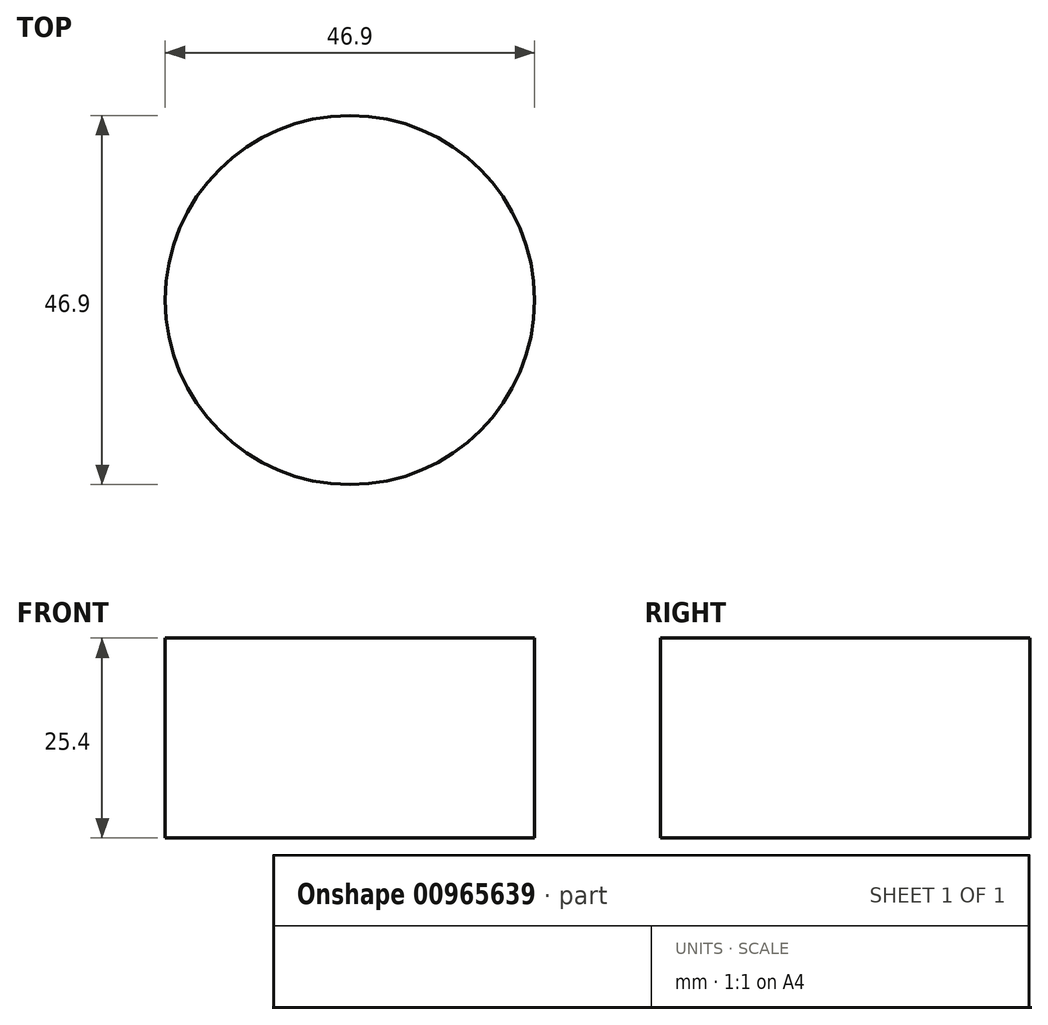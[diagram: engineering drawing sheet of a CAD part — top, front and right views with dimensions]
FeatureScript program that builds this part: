
annotation { "Feature Type Name" : "Feature", "Feature Type Description" : "" }
export const myFeature = defineFeature(function(context is Context, id is Id, definition is map)
    precondition{}
    {
        {
            var Q0;
            Q0=qCreatedBy(makeId("Top.planeOp"),FACE);
            var sketch = newSketch(context, id + "F0", { "sketchPlane" : qUnion([Q0])});
            skCircle(sketch, "E0", {"center": v(0, 0) * mm, "radius": 23.45 * mm});
            skSolve(sketch);
        }
        {
            var Q0;
            Q0=makeQuery(id+"F0.imprint","IMPRINT",FACE,{"disambiguationData":[TD([[makeQuery(id+"F0.imprint","IMPRINT",EDGE,{"derivedFrom":sQuery(id+"F0.wireOp",EDGE,"E0")}),1.0]])]});
            extrude(context, id + "F1", {"entities" : qUnion([Q0]), "oppositeDirection" : true, "depth" : 25.4 * mm, "offsetDistance" : 25.4 * mm});
        }
    });
